# Revit family: Sanitary_Accessories_DURAVIT-AG_Starck-T-Toilet-paper-holder-255x76x50-mm-009938
name_source: partatom
category: Generic Models
revit_build: Autodesk Revit 2018 (Build: 20190510_1515(x64)
units: mm (PartAtom-declared; Revit-internal decimal feet)

## family parameters
Can host rebar = No
Cut with Voids When Loaded = No
Host = Face
OmniClass Number = 23.31.19.00
OmniClass Title = Toilets
Part Type = Normal
Room Calculation Point = No
Round Connector Dimension = Use Diameter
Shared = No

## types (2) — shared parameters
BIMobject category = Bathroom Accessories
Default Elevation = 1219 mm
Design country = Germany
ETIM classification = EC010553 | Toilet roll holder
Edition number = 1
IFC Classification = Furnishing Element
Installation instructions = https://pro.duravit.com
Manufacturer = Duravit
Manufacturer country = Germany
Manufacturer name = DURAVIT AG
Masterformat 2014 Code = 01 52 19
Masterformat 2014 Description = Sanitary Facilities
Material main = Brass
Model = Starck T Toilet paper holder 255x76x50 mm - 009938
OmniClass Code = 23-31 19 00
OmniClass Description = Toilets
Product Guid = 5a95245d-4838-4a8e-b6a1-af667aba4eac
Product SKU = Starck-T-Toilet-paper-holder-255x76x50-mm-009938
Product certification = https://pro.duravit.com
Product data url = https://bimobject.com
Product family = Starck T
Product group = Toilet paper holder
Product name = Starck T Toilet paper holder 255x76x50 mm - 009938
Product url = https://pro.duravit.com
QR code = https://bimobject.com
Technical description = https://pro.duravit.com
UNSPSC Code = 301815
URL = https://www.duravit.com
Uniclass 2015 Code = Pr_40_20_93
Uniclass 2015 Name = Urinal and WC fittings
Uniformat II Code = D2030
Uniformat II Description = Sanitary Waste
Weight Net (Kg) = 0.24
Youtube clip = https://pro.duravit.com

## per-type parameters (varying)
| type | Description | Main material |
| 10 - Chrome | Duravit Starck T Toilet paper holder Chrome 255x76x50 mm - 0099381000 | Duravit - Metal - 10 - Chrome |
| 46 - Black Matt | Duravit Starck T Toilet paper holder Black Matt 255x76x50 mm - 0099384600 | Duravit - Metal - 46 - Black Matt |

## geometry (parser evidence)
native form markers: Sweep x4
no freeform markers — native parametric forms only
